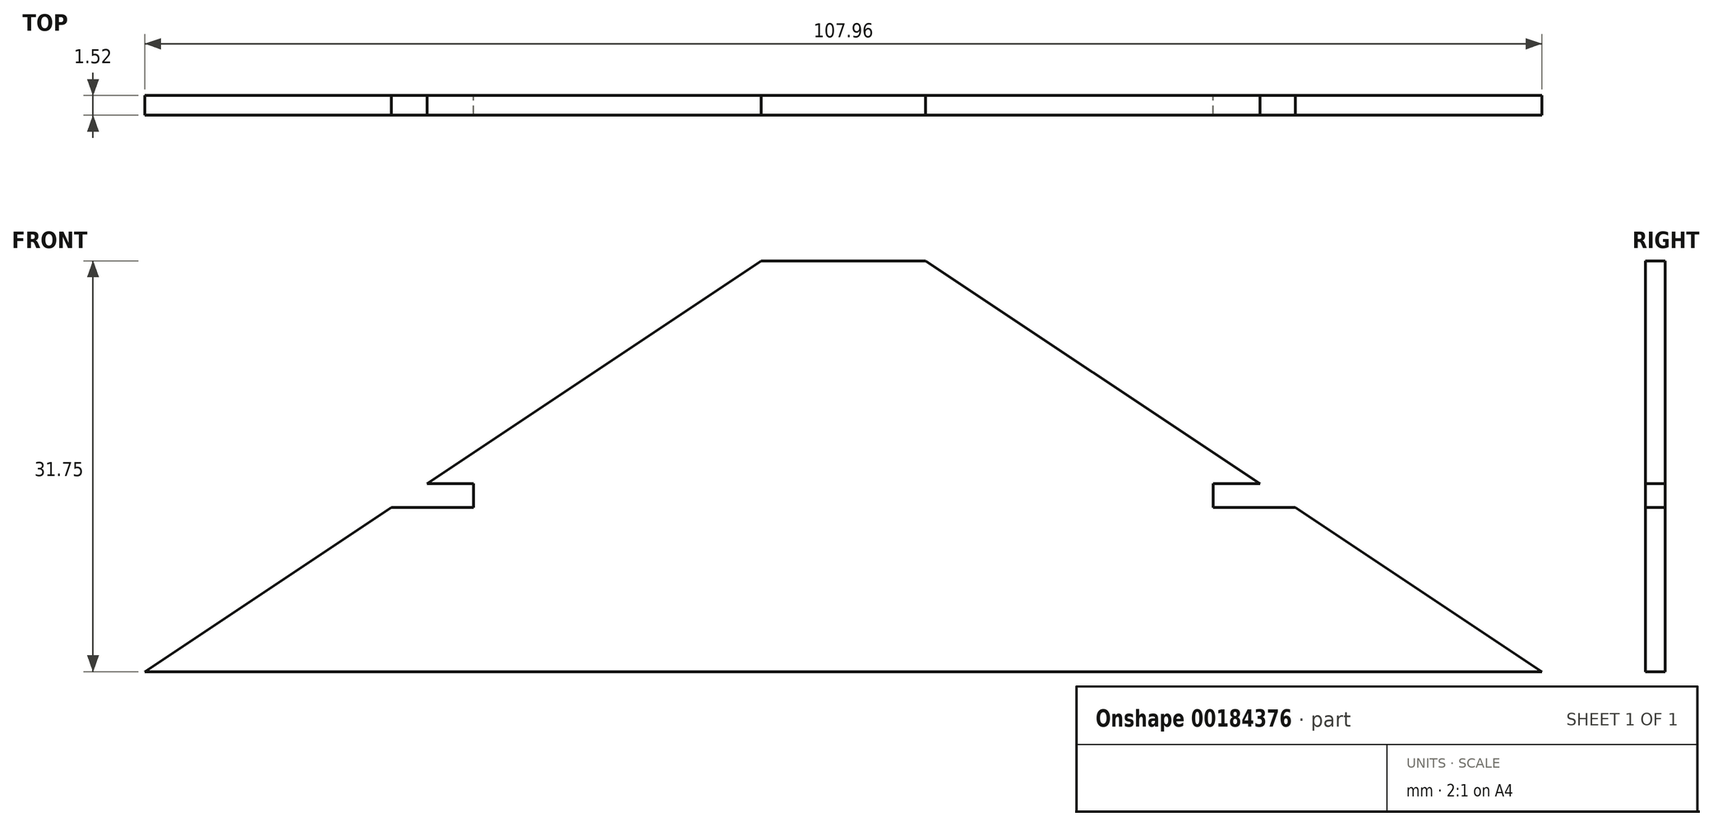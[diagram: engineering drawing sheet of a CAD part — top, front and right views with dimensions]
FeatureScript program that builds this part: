
annotation { "Feature Type Name" : "Feature", "Feature Type Description" : "" }
export const myFeature = defineFeature(function(context is Context, id is Id, definition is map)
    precondition{}
    {
        {
            var Q0;
            Q0=qCreatedBy(makeId("Front.planeOp"),FACE);
            var sketch = newSketch(context, id + "F0", { "sketchPlane" : qUnion([Q0])});
            skLineSegment(sketch, "E0", {"start": v(-6.35, 31.75) * mm, "end": v(6.35, 31.75) * mm});
            skLineSegment(sketch, "E1", {"start": v(6.35, 31.75) * mm, "end": v(53.97, 0) * mm});
            skLineSegment(sketch, "E2", {"start": v(53.97, 0) * mm, "end": v(-53.97, 0) * mm});
            skLineSegment(sketch, "E3", {"start": v(-53.98, 0) * mm, "end": v(-6.35, 31.75) * mm});
            skLineSegment(sketch, "E4", {"start": v(-32.18, 14.53) * mm, "end": v(-28.57, 14.53) * mm});
            skLineSegment(sketch, "E5", {"start": v(-28.57, 14.53) * mm, "end": v(-28.57, 12.7) * mm});
            skLineSegment(sketch, "E6", {"start": v(-28.57, 12.7) * mm, "end": v(-34.92, 12.7) * mm});
            skLineSegment(sketch, "E7", {"start": v(32.18, 14.53) * mm, "end": v(28.57, 14.53) * mm});
            skLineSegment(sketch, "E8", {"start": v(28.57, 14.53) * mm, "end": v(28.57, 12.7) * mm});
            skLineSegment(sketch, "E9", {"start": v(28.57, 12.7) * mm, "end": v(34.92, 12.7) * mm});
            skLineSegment(sketch, "E10", {"start": v(-28.57, 12.7) * mm, "end": v(28.57, 12.7) * mm, "construction": true});
            skLineSegment(sketch, "E11", {"start": v(0, 31.75) * mm, "end": v(0, 0) * mm, "construction": true});
            skSolve(sketch);
        }
        {
            var Q0;
            {var subQ2=sQuery(id+"F0.wireOp",EDGE,"E0");Q0=makeQuery(id+"F0.imprint","IMPRINT",FACE,{"disambiguationData":[TD([[makeQuery(id+"F0.imprint","IMPRINT",EDGE,{"derivedFrom":subQ2}),-1.0]])]});}
            extrude(context, id + "F1", {"entities" : qUnion([Q0]), "depth" : 1.52 * mm});
        }
    });
